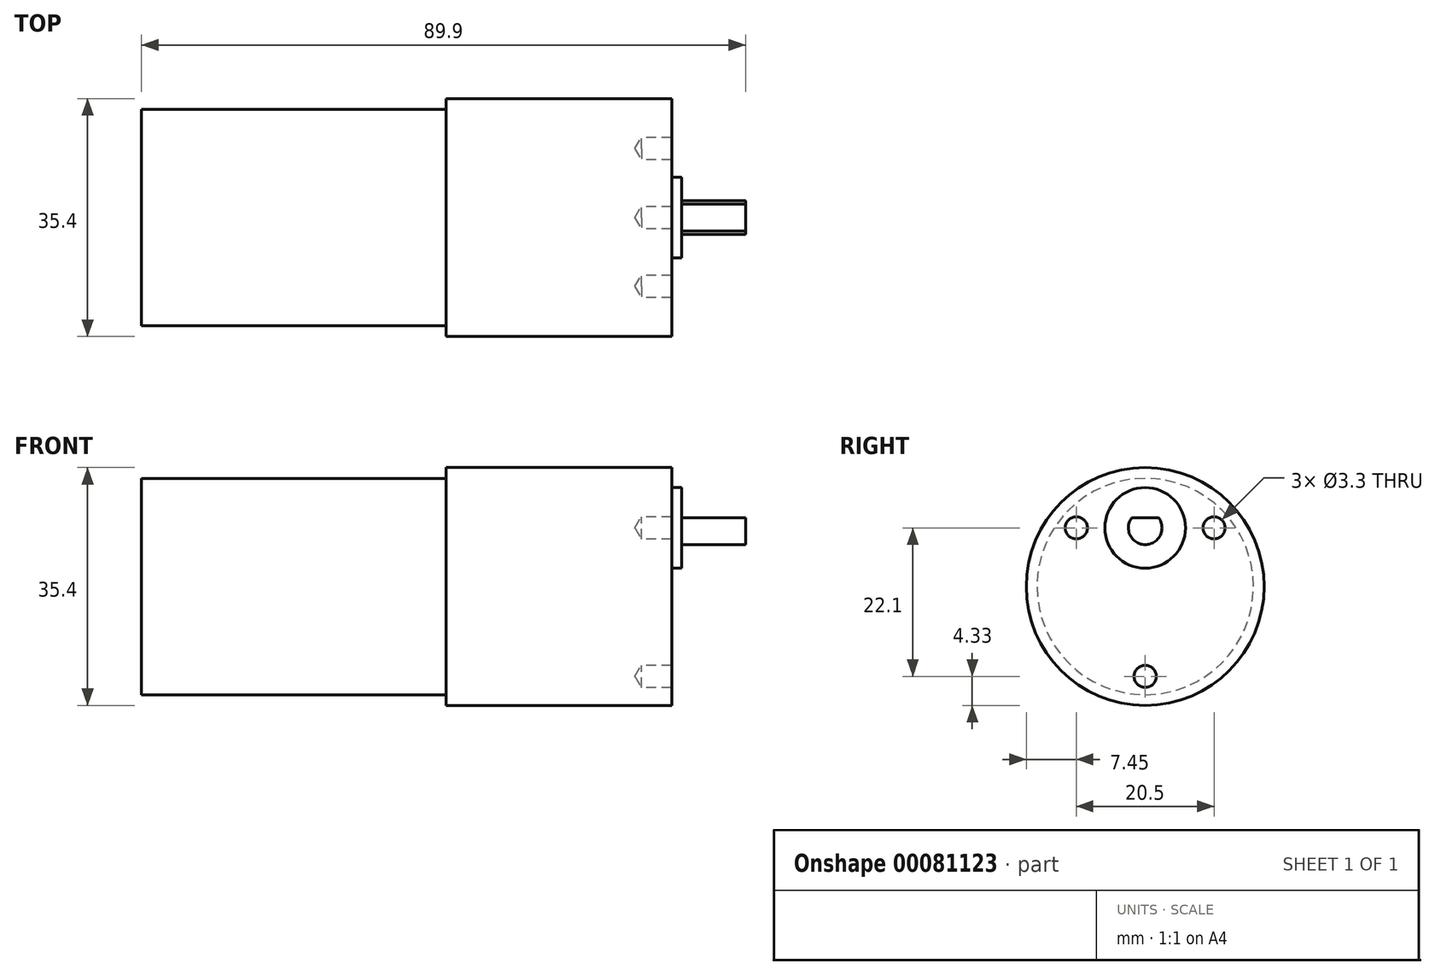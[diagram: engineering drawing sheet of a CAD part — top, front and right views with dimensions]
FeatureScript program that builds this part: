
annotation { "Feature Type Name" : "Feature", "Feature Type Description" : "" }
export const myFeature = defineFeature(function(context is Context, id is Id, definition is map)
    precondition{}
    {
        {
            var Q0;
            Q0=qCreatedBy(makeId("Front.planeOp"),FACE);
            var sketch = newSketch(context, id + "F0", { "sketchPlane" : qUnion([Q0])});
            skLineSegment(sketch, "E0", {"start": v(-78.9, 0) * mm, "end": v(-78.9, 16.1) * mm});
            skLineSegment(sketch, "E1", {"start": v(-78.9, 16.1) * mm, "end": v(-33.6, 16.1) * mm});
            skLineSegment(sketch, "E2", {"start": v(-33.6, 16.1) * mm, "end": v(-33.6, 17.7) * mm});
            skLineSegment(sketch, "E3", {"start": v(-33.6, 17.7) * mm, "end": v(0, 17.7) * mm});
            skLineSegment(sketch, "E4", {"start": v(0, 17.7) * mm, "end": v(0, 0) * mm});
            skLineSegment(sketch, "E5", {"start": v(0, 0) * mm, "end": v(-78.9, 0) * mm});
            skSolve(sketch);
        }
        {
            var Q0;
            Q0=makeQuery(id+"F0.imprint","IMPRINT",FACE,{"disambiguationData":[TD([[makeQuery(id+"F0.imprint","IMPRINT",EDGE,{"derivedFrom":sQuery(id+"F0.wireOp",EDGE,"E0")}),-1.0]])]});
            var Q1;
            Q1=sQuery(id+"F0.wireOp",EDGE,"E5");
            revolve(context, id + "F1", {"entities" : qUnion([Q0]), "axis" : qUnion([Q1]), "revolveType" : RevolveType.FULL});
        }
        {
            var Q0;
            Q0=makeQuery(id+"F1.opRevolve","SWEPT_FACE",FACE,{"disambiguationData":[OSD([sQuery(id+"F0.wireOp",EDGE,"E4")])]});
            var sketch = newSketch(context, id + "F2", { "sketchPlane" : qUnion([Q0])});
            skCircle(sketch, "E6", {"center": v(0, 8.73) * mm, "radius": 6 * mm});
            skPoint(sketch, "E7", {"position": v(-10.25, 8.73) * mm});
            skPoint(sketch, "E8.MirrorP", {"position": v(10.25, 8.73) * mm});
            skPoint(sketch, "E9", {"position": v(0, -13.37) * mm});
            skSolve(sketch);
        }
        {
            var Q0;
            Q0=makeQuery(id+"F2.imprint","IMPRINT",FACE,{"disambiguationData":[TD([[makeQuery(id+"F2.imprint","IMPRINT",EDGE,{"derivedFrom":sQuery(id+"F2.wireOp",EDGE,"E6")}),1.0]])]});
            extrude(context, id + "F3", {"entities" : qUnion([Q0]), "operationType" : NewBodyOperationType.ADD, "depth" : 1.5 * mm});
        }
        {
            var Q0;
            Q0=makeQuery(id+"F3.opExtrude","CAP_FACE",FACE,{"disambiguationData":[OSD([sQuery(id+"F2.wireOp",EDGE,"E6")])],"isStart":false});
            var sketch = newSketch(context, id + "F4", { "sketchPlane" : qUnion([Q0])});
            skArc(sketch, "E10", {"start": v(-2, 10.23) * mm, "mid": v(0, 6.23) * mm, "end": v(2, 10.23) * mm});
            skLineSegment(sketch, "E11", {"start": v(-2, 10.23) * mm, "end": v(2, 10.23) * mm});
            skSolve(sketch);
        }
        {
            var Q0;
            Q0=makeQuery(id+"F4.imprint","IMPRINT",FACE,{"disambiguationData":[TD([[makeQuery(id+"F4.imprint","IMPRINT",EDGE,{"derivedFrom":sQuery(id+"F4.wireOp",EDGE,"E10")}),1.0]])]});
            extrude(context, id + "F5", {"entities" : qUnion([Q0]), "operationType" : NewBodyOperationType.ADD, "depth" : 9.5 * mm});
        }
        {
            var Q0;
            Q0=sQuery(id+"F2.wireOp",VERTEX,"E7");
            var Q1;
            Q1=sQuery(id+"F2.wireOp",VERTEX,"E8.MirrorP");
            var Q2;
            Q2=sQuery(id+"F2.wireOp",VERTEX,"E9");
            var Q3;
            Q3=makeQuery(id+"F1.opRevolve","SWEPT_BODY",BODY,{"disambiguationData":[OSD([sQuery(id+"F0.wireOp",EDGE,"E0"),sQuery(id+"F0.wireOp",EDGE,"E1"),sQuery(id+"F0.wireOp",EDGE,"E2"),sQuery(id+"F0.wireOp",EDGE,"E3"),sQuery(id+"F0.wireOp",EDGE,"E4"),sQuery(id+"F0.wireOp",EDGE,"E5")])]});
            hole(context, id + "F6", {"style" : HoleStyle.SIMPLE, "endStyle" : HoleEndStyle.BLIND, "standardTappedOrClearance" : lookupTablePath({ "standard" : "ISO", "fit" : "Normal", "size" : "M3", "type" : "Clearance" }), "standardBlindInLast" : lookupTablePath({ "fit" : "Standard", "standard" : "ISO", "size" : "M3", "type" : "Clearance" }), "holeDiameter" : 3.3 * mm, "holeDepth" : 4.5 * mm, "startFromSketch" : true, "locations" : qUnion([Q0, Q1, Q2]), "scope" : qUnion([Q3])});
        }
    });
